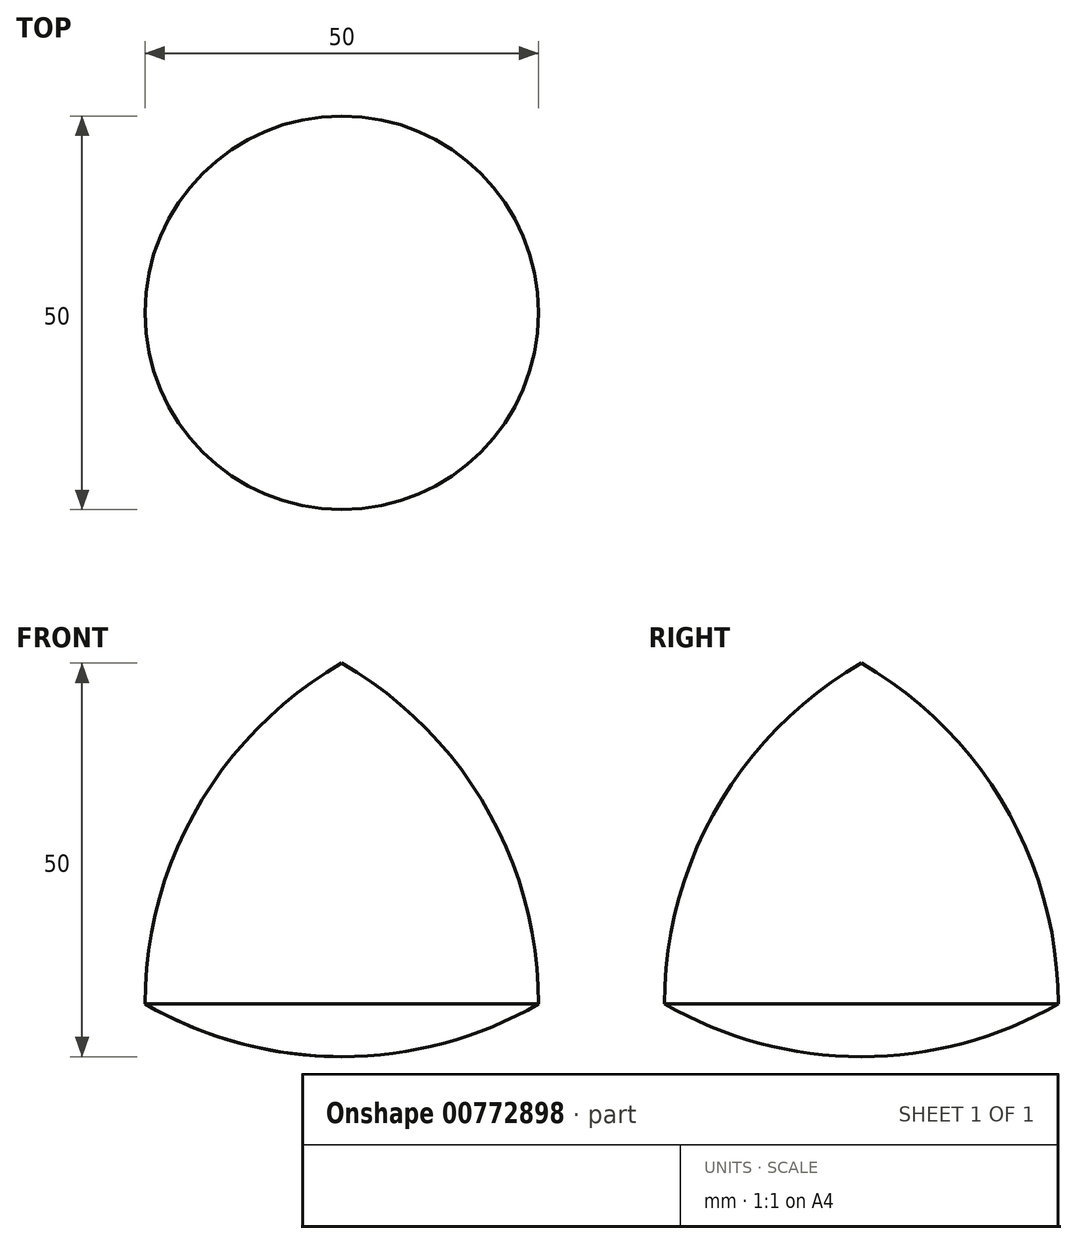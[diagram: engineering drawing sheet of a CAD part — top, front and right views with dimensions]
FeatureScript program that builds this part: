
annotation { "Feature Type Name" : "Feature", "Feature Type Description" : "" }
export const myFeature = defineFeature(function(context is Context, id is Id, definition is map)
    precondition{}
    {
        {
            var Q0;
            Q0=qCreatedBy(makeId("Front.planeOp"),FACE);
            var sketch = newSketch(context, id + "F0", { "sketchPlane" : qUnion([Q0])});
            skLineSegment(sketch, "E0", {"start": v(-25, 0) * mm, "end": v(25, 0) * mm, "construction": true});
            skLineSegment(sketch, "E1", {"start": v(25, 0) * mm, "end": v(0, 43.3) * mm, "construction": true});
            skLineSegment(sketch, "E2", {"start": v(0, 43.3) * mm, "end": v(-25, 0) * mm, "construction": true});
            skArc(sketch, "E3", {"start": v(0, 43.3) * mm, "mid": v(-18.3, 25) * mm, "end": v(-25, 0) * mm});
            skArc(sketch, "E4", {"start": v(-25, 0) * mm, "mid": v(0, -6.7) * mm, "end": v(25, 0) * mm});
            skArc(sketch, "E5", {"start": v(25, 0) * mm, "mid": v(18.3, 25) * mm, "end": v(0, 43.3) * mm});
            skLineSegment(sketch, "E6", {"start": v(0, 43.3) * mm, "end": v(0, -6.7) * mm});
            skSolve(sketch);
        }
        {
            var Q0;
            {var subQ0=sQuery(id+"F0.wireOp",EDGE,"E3");Q0=makeQuery(id+"F0.imprint","IMPRINT",FACE,{"disambiguationData":[TD([[makeQuery(id+"F0.imprint","IMPRINT",EDGE,{"derivedFrom":subQ0}),1.0]])]});}
            var Q1;
            Q1=sQuery(id+"F0.wireOp",EDGE,"E6");
            revolve(context, id + "F1", {"surfaceOperationType" : NewSurfaceOperationType.NEW, "entities" : qUnion([Q0]), "axis" : qUnion([Q1]), "revolveType" : RevolveType.FULL});
        }
    });
